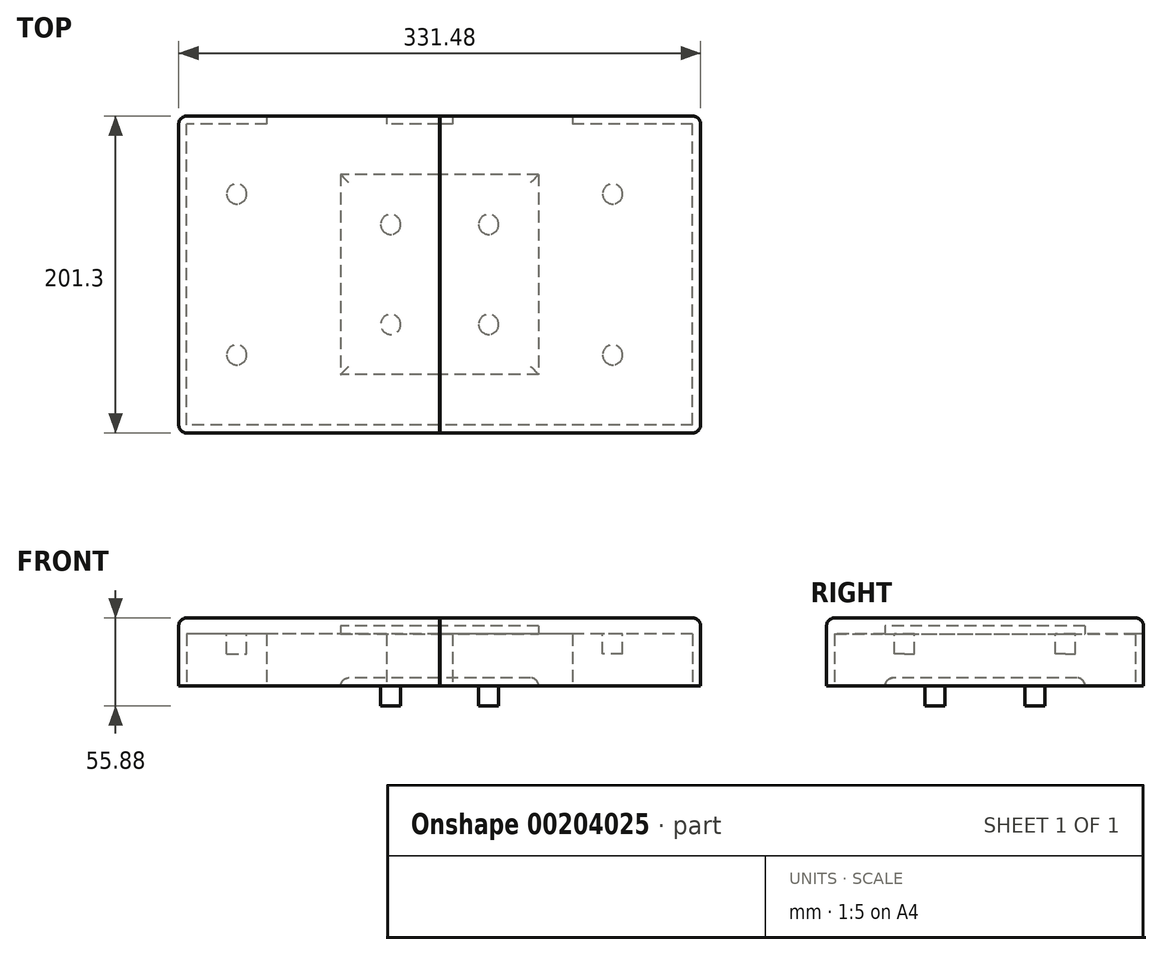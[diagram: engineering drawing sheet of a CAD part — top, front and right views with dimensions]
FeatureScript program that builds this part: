
annotation { "Feature Type Name" : "Feature", "Feature Type Description" : "" }
export const myFeature = defineFeature(function(context is Context, id is Id, definition is map)
    precondition{}
    {
        {
            var Q0;
            Q0=qCreatedBy(makeId("Top.planeOp"),FACE);
            var sketch = newSketch(context, id + "F0", { "sketchPlane" : qUnion([Q0])});
            skLineSegment(sketch, "E0.bottom", {"start": v(160.66, -95.57) * mm, "end": v(-160.66, -95.57) * mm});
            skLineSegment(sketch, "E0.top", {"start": v(160.66, 95.57) * mm, "end": v(-160.66, 95.57) * mm});
            skLineSegment(sketch, "E0.left", {"start": v(160.66, -95.57) * mm, "end": v(160.66, 95.57) * mm});
            skLineSegment(sketch, "E0.right", {"start": v(-160.66, -95.57) * mm, "end": v(-160.66, 95.57) * mm});
            skPoint(sketch, "E0.middle", {"position": v(0, 0) * mm});
            skSolve(sketch);
        }
        {
            var Q0;
            Q0 = qSketchRegion(id + "F0", true);
            extrude(context, id + "F1", {"entities" : qUnion([Q0]), "depth" : 38.1 * mm});
        }
        {
            var Q0;
            Q0=makeQuery(id+"F1.opExtrude","CAP_FACE",FACE,{"disambiguationData":[OSD([sQuery(id+"F0.wireOp",EDGE,"E0.bottom"),sQuery(id+"F0.wireOp",EDGE,"E0.top"),sQuery(id+"F0.wireOp",EDGE,"E0.left"),sQuery(id+"F0.wireOp",EDGE,"E0.right")])],"isStart":true});
            shell(context, id + "F2", {"entities" : qUnion([Q0]), "thickness" : 5.08 * mm, "oppositeDirection" : true});
        }
        {
            var Q0;
            Q0=makeQuery(id+"F2.opShell","OFFSET_FACE",FACE,{"disambiguationData":[OSD([sQuery(id+"F0.wireOp",EDGE,"E0.bottom"),sQuery(id+"F0.wireOp",EDGE,"E0.top"),sQuery(id+"F0.wireOp",EDGE,"E0.left"),sQuery(id+"F0.wireOp",EDGE,"E0.right")])]});
            extrude(context, id + "F3", {"entities" : qUnion([Q0]), "operationType" : NewBodyOperationType.ADD, "depth" : 5.08 * mm});
        }
        {
            var Q0;
            Q0=qCreatedBy(makeId("Top.planeOp"),FACE);
            var sketch = newSketch(context, id + "F4", { "sketchPlane" : qUnion([Q0])});
            skLineSegment(sketch, "E1.bottom", {"start": v(62.87, 63.5) * mm, "end": v(-62.87, 63.5) * mm});
            skLineSegment(sketch, "E1.top", {"start": v(62.87, -63.5) * mm, "end": v(-62.87, -63.5) * mm});
            skLineSegment(sketch, "E1.left", {"start": v(62.87, 63.5) * mm, "end": v(62.87, -63.5) * mm});
            skLineSegment(sketch, "E1.right", {"start": v(-62.87, 63.5) * mm, "end": v(-62.87, -63.5) * mm});
            skPoint(sketch, "E1.middle", {"position": v(0, 0) * mm});
            skSolve(sketch);
        }
        {
            var Q0;
            Q0 = qSketchRegion(id + "F4", true);
            extrude(context, id + "F5", {"entities" : qUnion([Q0]), "depth" : 5.08 * mm});
        }
        {
            var Q0;
            Q0=makeQuery(id+"F5.opExtrude","CAP_FACE",FACE,{"disambiguationData":[OSD([sQuery(id+"F4.wireOp",EDGE,"E1.bottom"),sQuery(id+"F4.wireOp",EDGE,"E1.top"),sQuery(id+"F4.wireOp",EDGE,"E1.left"),sQuery(id+"F4.wireOp",EDGE,"E1.right")])],"isStart":false});
            extrude(context, id + "F6", {"entities" : qUnion([Q0]), "operationType" : NewBodyOperationType.REMOVE, "depth" : 33.02 * mm});
        }
        {
            var Q0;
            Q0=makeQuery(id+"F2.opShell","OFFSET_FACE",FACE,{"disambiguationData":[OSD([sQuery(id+"F0.wireOp",EDGE,"E0.top")])]});
            var sketch = newSketch(context, id + "F7", { "sketchPlane" : qUnion([Q0])});
            skLineSegment(sketch, "E2.bottom", {"start": v(-109.86, 33.02) * mm, "end": v(-33.66, 33.02) * mm});
            skLineSegment(sketch, "E2.top", {"start": v(-109.86, 0) * mm, "end": v(-33.66, 0) * mm});
            skLineSegment(sketch, "E2.left", {"start": v(-109.86, 33.02) * mm, "end": v(-109.86, 0) * mm});
            skLineSegment(sketch, "E2.right", {"start": v(-33.66, 33.02) * mm, "end": v(-33.66, 0) * mm});
            skSolve(sketch);
        }
        {
            var Q0;
            Q0 = qSketchRegion(id + "F7", true);
            extrude(context, id + "F8", {"entities" : qUnion([Q0]), "operationType" : NewBodyOperationType.REMOVE, "oppositeDirection" : true, "depth" : 25.4 * mm});
        }
        {
            var Q0;
            {var subQ1=sQuery(id+"F0.wireOp",EDGE,"E0.left");var subQ2=sQuery(id+"F0.wireOp",EDGE,"E0.top");Q0=makeQuery(id+"F8.boolean.opBoolean","SPLIT",FACE,{"disambiguationData":[TD([makeQuery(id+"F2.opShell","OFFSET_FACE",FACE,{"disambiguationData":[OSD([subQ1])]})])],"derivedFrom":makeQuery(id+"F2.opShell","OFFSET_FACE",FACE,{"disambiguationData":[OSD([subQ2])]})});}
            var sketch = newSketch(context, id + "F9", { "sketchPlane" : qUnion([Q0])});
            skLineSegment(sketch, "E3.bottom", {"start": v(8.26, 33.02) * mm, "end": v(84.46, 33.02) * mm});
            skLineSegment(sketch, "E3.top", {"start": v(8.26, 0) * mm, "end": v(84.46, 0) * mm});
            skLineSegment(sketch, "E3.left", {"start": v(8.26, 33.02) * mm, "end": v(8.26, 0) * mm});
            skLineSegment(sketch, "E3.right", {"start": v(84.46, 33.02) * mm, "end": v(84.46, 0) * mm});
            skSolve(sketch);
        }
        {
            var Q0;
            Q0 = qSketchRegion(id + "F9", true);
            extrude(context, id + "F10", {"entities" : qUnion([Q0]), "operationType" : NewBodyOperationType.REMOVE, "oppositeDirection" : true, "depth" : 25.4 * mm});
        }
        {
            var Q0;
            Q0=makeQuery(id+"F5.opExtrude","CAP_EDGE",EDGE,{"disambiguationData":[OSD([sQuery(id+"F4.wireOp",EDGE,"E1.right")])],"isStart":false});
            var Q1;
            Q1=makeQuery(id+"F5.opExtrude","CAP_EDGE",EDGE,{"disambiguationData":[OSD([sQuery(id+"F4.wireOp",EDGE,"E1.top")])],"isStart":false});
            var Q2;
            Q2=makeQuery(id+"F5.opExtrude","CAP_EDGE",EDGE,{"disambiguationData":[OSD([sQuery(id+"F4.wireOp",EDGE,"E1.left")])],"isStart":false});
            var Q3;
            Q3=makeQuery(id+"F5.opExtrude","CAP_EDGE",EDGE,{"disambiguationData":[OSD([sQuery(id+"F4.wireOp",EDGE,"E1.bottom")])],"isStart":false});
            fillet(context, id + "F11", {"entities" : qUnion([Q0, Q1, Q2, Q3]), "radius" : 5.08 * mm, "tangentPropagation" : true, "allowEdgeOverflow" : false});
        }
        {
            var Q0;
            Q0=makeQuery(id+"F10.boolean.opBoolean","MERGE",FACE,{"derivedFrom":[makeQuery(id+"F8.boolean.opBoolean","MERGE",FACE,{"derivedFrom":[makeQuery(id+"F3.opExtrude","CAP_FACE",FACE,{"disambiguationData":[OSD([sQuery(id+"F0.wireOp",EDGE,"E0.bottom"),sQuery(id+"F0.wireOp",EDGE,"E0.top"),sQuery(id+"F0.wireOp",EDGE,"E0.left"),sQuery(id+"F0.wireOp",EDGE,"E0.right")])],"isStart":false}),makeQuery(id+"F8.opExtrude","SWEPT_FACE",FACE,{"disambiguationData":[OSD([sQuery(id+"F7.wireOp",EDGE,"E2.bottom")])]})]}),makeQuery(id+"F10.opExtrude","SWEPT_FACE",FACE,{"disambiguationData":[OSD([sQuery(id+"F9.wireOp",EDGE,"E3.bottom")])]})]});
            var sketch = newSketch(context, id + "F12", { "sketchPlane" : qUnion([Q0])});
            skCircle(sketch, "E4", {"center": v(-128.9, 51.12) * mm, "radius": 6.35 * mm});
            skSolve(sketch);
        }
        {
            var Q0;
            Q0 = qSketchRegion(id + "F12", true);
            extrude(context, id + "F13", {"entities" : qUnion([Q0]), "operationType" : NewBodyOperationType.ADD, "depth" : 12.7 * mm});
        }
        {
            var Q0;
            Q0=makeQuery(id+"F10.boolean.opBoolean","MERGE",FACE,{"derivedFrom":[makeQuery(id+"F8.boolean.opBoolean","MERGE",FACE,{"derivedFrom":[makeQuery(id+"F3.opExtrude","CAP_FACE",FACE,{"disambiguationData":[OSD([sQuery(id+"F0.wireOp",EDGE,"E0.bottom"),sQuery(id+"F0.wireOp",EDGE,"E0.top"),sQuery(id+"F0.wireOp",EDGE,"E0.left"),sQuery(id+"F0.wireOp",EDGE,"E0.right")])],"isStart":false}),makeQuery(id+"F8.opExtrude","SWEPT_FACE",FACE,{"disambiguationData":[OSD([sQuery(id+"F7.wireOp",EDGE,"E2.bottom")])]})]}),makeQuery(id+"F10.opExtrude","SWEPT_FACE",FACE,{"disambiguationData":[OSD([sQuery(id+"F9.wireOp",EDGE,"E3.bottom")])]})]});
            var sketch = newSketch(context, id + "F14", { "sketchPlane" : qUnion([Q0])});
            skCircle(sketch, "E5", {"center": v(-128.9, -51.12) * mm, "radius": 6.35 * mm});
            skSolve(sketch);
        }
        {
            var Q0;
            Q0 = qSketchRegion(id + "F14", true);
            extrude(context, id + "F15", {"entities" : qUnion([Q0]), "operationType" : NewBodyOperationType.ADD, "depth" : 12.7 * mm});
        }
        {
            var Q0;
            Q0=makeQuery(id+"F5.opExtrude","CAP_FACE",FACE,{"disambiguationData":[OSD([sQuery(id+"F4.wireOp",EDGE,"E1.bottom"),sQuery(id+"F4.wireOp",EDGE,"E1.top"),sQuery(id+"F4.wireOp",EDGE,"E1.left"),sQuery(id+"F4.wireOp",EDGE,"E1.right")])],"isStart":true});
            var sketch = newSketch(context, id + "F16", { "sketchPlane" : qUnion([Q0])});
            skCircle(sketch, "E6", {"center": v(-31.12, 31.75) * mm, "radius": 6.35 * mm});
            skCircle(sketch, "E7.MirrorC", {"center": v(31.12, 31.75) * mm, "radius": 6.35 * mm});
            skCircle(sketch, "E8.MirrorC", {"center": v(-31.12, -31.75) * mm, "radius": 6.35 * mm});
            skCircle(sketch, "E9.MirrorC", {"center": v(31.12, -31.75) * mm, "radius": 6.35 * mm});
            skSolve(sketch);
        }
        {
            var Q0;
            Q0 = qSketchRegion(id + "F16", true);
            extrude(context, id + "F17", {"entities" : qUnion([Q0]), "operationType" : NewBodyOperationType.ADD, "depth" : 12.7 * mm});
        }
        {
            var Q0;
            Q0=makeQuery(id+"F10.boolean.opBoolean","MERGE",FACE,{"derivedFrom":[makeQuery(id+"F8.boolean.opBoolean","MERGE",FACE,{"derivedFrom":[makeQuery(id+"F3.opExtrude","CAP_FACE",FACE,{"disambiguationData":[OSD([sQuery(id+"F0.wireOp",EDGE,"E0.bottom"),sQuery(id+"F0.wireOp",EDGE,"E0.top"),sQuery(id+"F0.wireOp",EDGE,"E0.left"),sQuery(id+"F0.wireOp",EDGE,"E0.right")])],"isStart":false}),makeQuery(id+"F8.opExtrude","SWEPT_FACE",FACE,{"disambiguationData":[OSD([sQuery(id+"F7.wireOp",EDGE,"E2.bottom")])]})]}),makeQuery(id+"F10.opExtrude","SWEPT_FACE",FACE,{"disambiguationData":[OSD([sQuery(id+"F9.wireOp",EDGE,"E3.bottom")])]})]});
            var sketch = newSketch(context, id + "F18", { "sketchPlane" : qUnion([Q0])});
            skCircle(sketch, "E10", {"center": v(109.86, 51.12) * mm, "radius": 6.35 * mm});
            skCircle(sketch, "E11.MirrorC", {"center": v(109.86, -51.12) * mm, "radius": 6.35 * mm});
            skSolve(sketch);
        }
        {
            var Q0;
            Q0 = qSketchRegion(id + "F18", true);
            extrude(context, id + "F19", {"entities" : qUnion([Q0]), "operationType" : NewBodyOperationType.ADD, "depth" : 12.7 * mm});
        }
        {
            var Q0;
            Q0=makeQuery(id+"F5.opExtrude","CAP_FACE",FACE,{"disambiguationData":[OSD([sQuery(id+"F4.wireOp",EDGE,"E1.bottom"),sQuery(id+"F4.wireOp",EDGE,"E1.top"),sQuery(id+"F4.wireOp",EDGE,"E1.left"),sQuery(id+"F4.wireOp",EDGE,"E1.right")])],"isStart":true});
            var sketch = newSketch(context, id + "F20", { "sketchPlane" : qUnion([Q0])});
            skLineSegment(sketch, "E12.bottom", {"start": v(0.13, 127) * mm, "end": v(-0.13, 127) * mm});
            skLineSegment(sketch, "E12.top", {"start": v(0.13, -127) * mm, "end": v(-0.13, -127) * mm});
            skLineSegment(sketch, "E12.left", {"start": v(0.13, 127) * mm, "end": v(0.13, -127) * mm});
            skLineSegment(sketch, "E12.right", {"start": v(-0.13, 127) * mm, "end": v(-0.13, -127) * mm});
            skPoint(sketch, "E12.middle", {"position": v(0, 0) * mm});
            skSolve(sketch);
        }
        {
            var Q0;
            Q0 = qSketchRegion(id + "F20", true);
            extrude(context, id + "F21", {"entities" : qUnion([Q0]), "operationType" : NewBodyOperationType.REMOVE, "oppositeDirection" : true, "depth" : 76.2 * mm});
        }
        {
            var Q0;
            Q0=makeQuery(id+"F1.opExtrude","CAP_EDGE",EDGE,{"disambiguationData":[OSD([sQuery(id+"F0.wireOp",EDGE,"E0.right")])],"isStart":false});
            var Q1;
            {var subQ0=sQuery(id+"F0.wireOp",EDGE,"E0.right");var subQ1=sQuery(id+"F0.wireOp",EDGE,"E0.top");Q1=makeQuery(id+"F21.boolean.opBoolean","SPLIT",EDGE,{"disambiguationData":[TD([makeQuery(id+"F1.opExtrude","SWEPT_FACE",FACE,{"disambiguationData":[OSD([subQ0])]})])],"derivedFrom":makeQuery(id+"F1.opExtrude","CAP_EDGE",EDGE,{"disambiguationData":[OSD([subQ1])],"isStart":false})});}
            var Q2;
            {var subQ0=sQuery(id+"F0.wireOp",EDGE,"E0.bottom");var subQ1=sQuery(id+"F0.wireOp",EDGE,"E0.right");Q2=makeQuery(id+"F21.boolean.opBoolean","SPLIT",EDGE,{"disambiguationData":[TD([makeQuery(id+"F1.opExtrude","SWEPT_FACE",FACE,{"disambiguationData":[OSD([subQ1])]})])],"derivedFrom":makeQuery(id+"F1.opExtrude","CAP_EDGE",EDGE,{"disambiguationData":[OSD([subQ0])],"isStart":false})});}
            var Q3;
            {var subQ0=sQuery(id+"F0.wireOp",EDGE,"E0.bottom");var subQ1=sQuery(id+"F0.wireOp",EDGE,"E0.left");Q3=makeQuery(id+"F21.boolean.opBoolean","SPLIT",EDGE,{"disambiguationData":[TD([makeQuery(id+"F1.opExtrude","SWEPT_FACE",FACE,{"disambiguationData":[OSD([subQ1])]})])],"derivedFrom":makeQuery(id+"F1.opExtrude","CAP_EDGE",EDGE,{"disambiguationData":[OSD([subQ0])],"isStart":false})});}
            var Q4;
            {var subQ0=sQuery(id+"F0.wireOp",EDGE,"E0.left");var subQ1=sQuery(id+"F0.wireOp",EDGE,"E0.top");Q4=makeQuery(id+"F21.boolean.opBoolean","SPLIT",EDGE,{"disambiguationData":[TD([makeQuery(id+"F1.opExtrude","SWEPT_FACE",FACE,{"disambiguationData":[OSD([subQ0])]})])],"derivedFrom":makeQuery(id+"F1.opExtrude","CAP_EDGE",EDGE,{"disambiguationData":[OSD([subQ1])],"isStart":false})});}
            var Q5;
            Q5=makeQuery(id+"F1.opExtrude","CAP_EDGE",EDGE,{"disambiguationData":[OSD([sQuery(id+"F0.wireOp",EDGE,"E0.left")])],"isStart":false});
            fillet(context, id + "F22", {"entities" : qUnion([Q0, Q1, Q2, Q3, Q4, Q5]), "radius" : 5.08 * mm, "tangentPropagation" : true, "allowEdgeOverflow" : false});
        }
        {
            var Q0;
            Q0=makeQuery(id+"F1.opExtrude","SWEPT_EDGE",EDGE,{"disambiguationData":[OSD([sQuery(id+"F0.wireOp",EDGE,"E0.bottom"),sQuery(id+"F0.wireOp",EDGE,"E0.right")])]});
            var Q1;
            Q1=makeQuery(id+"F1.opExtrude","SWEPT_EDGE",EDGE,{"disambiguationData":[OSD([sQuery(id+"F0.wireOp",EDGE,"E0.top"),sQuery(id+"F0.wireOp",EDGE,"E0.right")])]});
            var Q2;
            Q2=makeQuery(id+"F1.opExtrude","SWEPT_EDGE",EDGE,{"disambiguationData":[OSD([sQuery(id+"F0.wireOp",EDGE,"E0.bottom"),sQuery(id+"F0.wireOp",EDGE,"E0.left")])]});
            var Q3;
            Q3=makeQuery(id+"F1.opExtrude","SWEPT_EDGE",EDGE,{"disambiguationData":[OSD([sQuery(id+"F0.wireOp",EDGE,"E0.top"),sQuery(id+"F0.wireOp",EDGE,"E0.left")])]});
            fillet(context, id + "F23", {"entities" : qUnion([Q0, Q1, Q2, Q3]), "radius" : 5.08 * mm, "tangentPropagation" : true, "allowEdgeOverflow" : false});
        }
    });
